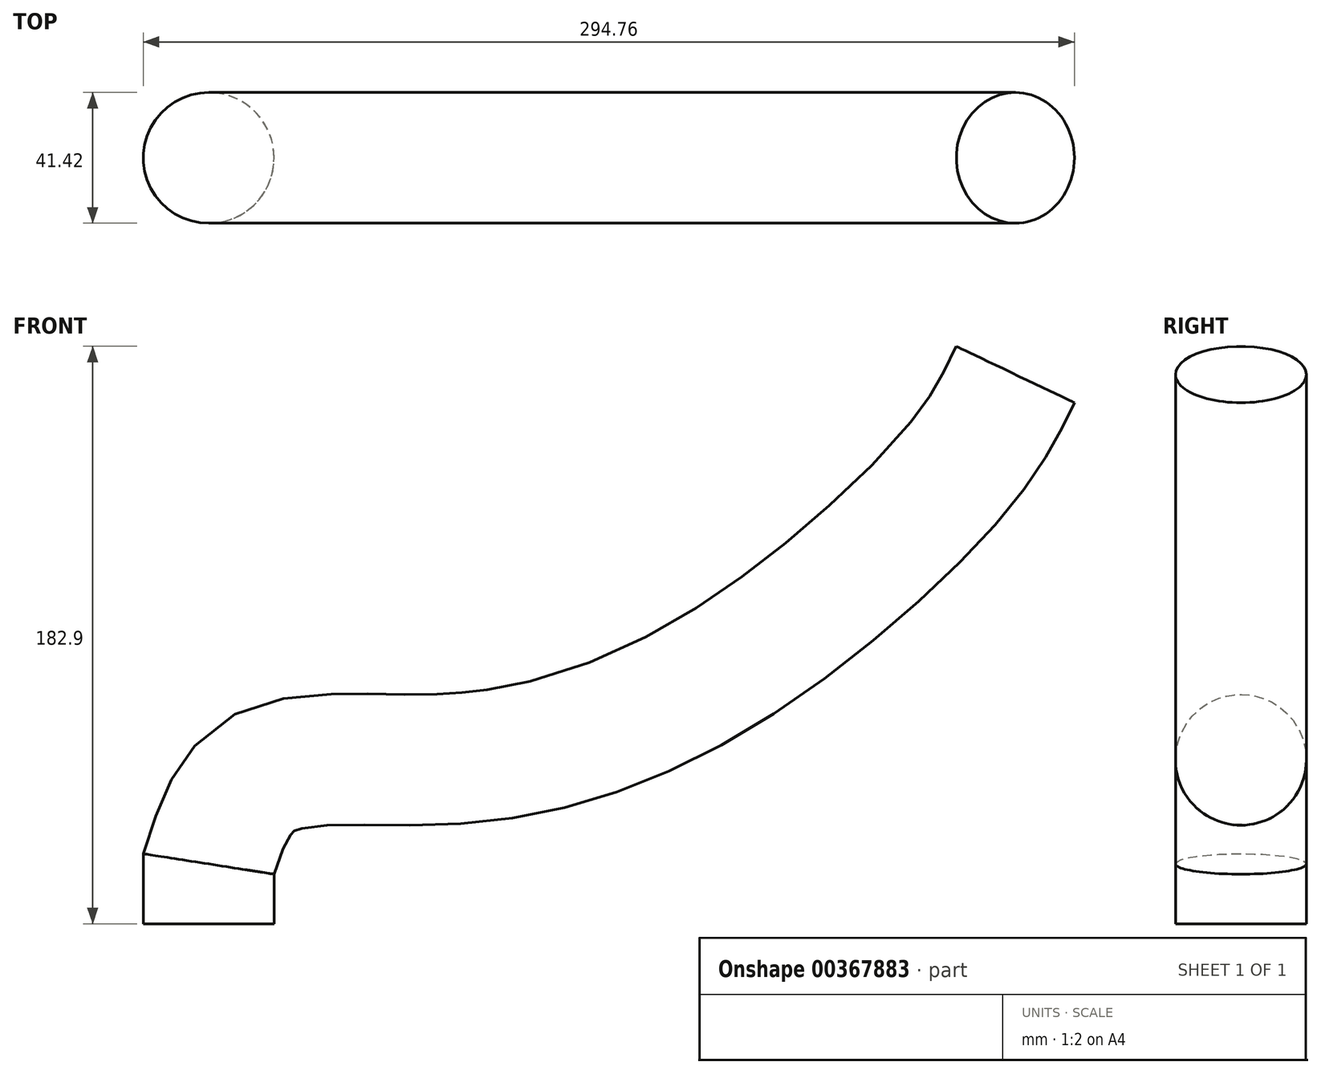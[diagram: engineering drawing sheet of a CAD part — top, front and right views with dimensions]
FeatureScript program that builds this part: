
annotation { "Feature Type Name" : "Feature", "Feature Type Description" : "" }
export const myFeature = defineFeature(function(context is Context, id is Id, definition is map)
    precondition{}
    {
        {
            var Q0;
            Q0=qCreatedBy(makeId("Front.planeOp"),FACE);
            var sketch = newSketch(context, id + "F0", { "sketchPlane" : qUnion([Q0])});
            skLineSegment(sketch, "E0", {"start": v(0, 0) * mm, "end": v(0, 18.95) * mm});
            skFitSpline(sketch, "E1", {"points": [v(0, 18.95) * mm, v(16.8, 47.37) * mm, v(74.07, 52.1) * mm, v(157.18, 77.51) * mm, v(237.7, 145.12) * mm, v(255.36, 173.97) * mm], "startDerivative": vector(74.34, 232.34) * mm, "endDerivative": vector(82.78, 173.25) * mm});
            skSolve(sketch);
        }
        {
            var Q0;
            Q0=qCreatedBy(makeId("Top.planeOp"),FACE);
            var sketch = newSketch(context, id + "F1", { "sketchPlane" : qUnion([Q0])});
            skCircle(sketch, "E2", {"center": v(0, 0) * mm, "radius": 20.71 * mm});
            skSolve(sketch);
        }
        {
            var Q0;
            Q0=makeQuery(id+"F1.imprint","IMPRINT",FACE,{"disambiguationData":[TD([[makeQuery(id+"F1.imprint","IMPRINT",EDGE,{"derivedFrom":sQuery(id+"F1.wireOp",EDGE,"E2")}),1.0]])]});
            var Q1;
            Q1=sQuery(id+"F0.wireOp",EDGE,"E0");
            var Q2;
            Q2=sQuery(id+"F0.wireOp",EDGE,"E1");
            sweep(context, id + "F2", {"profiles" : qUnion([Q0]), "path" : qUnion([Q1, Q2])});
        }
    });
